# Revit family: CLED
name_source: partatom
category: Lighting Fixtures
revit_build: Autodesk Revit 2014 (Build: 20130308_1515(x64)
units: mm (PartAtom-declared; Revit-internal decimal feet)

## types (1)
- CLED
    Apparent Load = 120 VA
    Assembly Code = D5020200
    Color Filter = 16777215
    Connector Description = Lighting Connector
    Default Elevation = 48"
    Description = Retrofit existing canopy (175w-400w) offering clean white
light giving greater visibility to each location
    Dimming Lamp Color Temperature Shift = <None>
    Drum-Height = 24"
    Emit Shape Visible in Rendering = No
    Emit from Rectangle Length = 15"
    Emit from Rectangle Width = 15"
    Features = Stylish vertically finned die-cast heat sink
• Designed for optimal thermal transfer and easy installation
• Made from low-copper marine-grade cast aluminum
• Optical assembly designed to exceed IP66 design stadards allowing for light
hose-down cleaning
• Thermal frame technology provides state-of-the-art passive cooling in the
most demanding environments
• 73 CRI standard
• Wet Location Listed
• Operating Temp: -40°C - 40°C
• Hub Requires 3 inch Recess for Surface Mounting
• Optional 0-10V dimming
    Fixture distribution = Direct
    Housing Material = Paint - Hubbell - Matte White
    Lamp = LED
    Length = 16"
    Load Classification = Lighting
    Manufacturer = Whiteway
    Model = CLED
    Photometric Web File = CLED-120W.ies
    Power Factor = 1
    Product Documentation Link = https://hubbellcdn.com
    Product Link = https://www.hubbell.com
    Reflector Finish = Hubbell - White Glass
    Tilt Angle = -90.00°
    URL = https://www.hubbell.com
    Voltage = 120 V
    Warranty = 5 years Warranty
    Wattage Comments = 120W
    Watts = 120 W
    Width = 16"
    Wings = Hubbell - White Glass

## geometry (parser evidence)
native form markers: Sweep x6
no freeform markers — native parametric forms only
